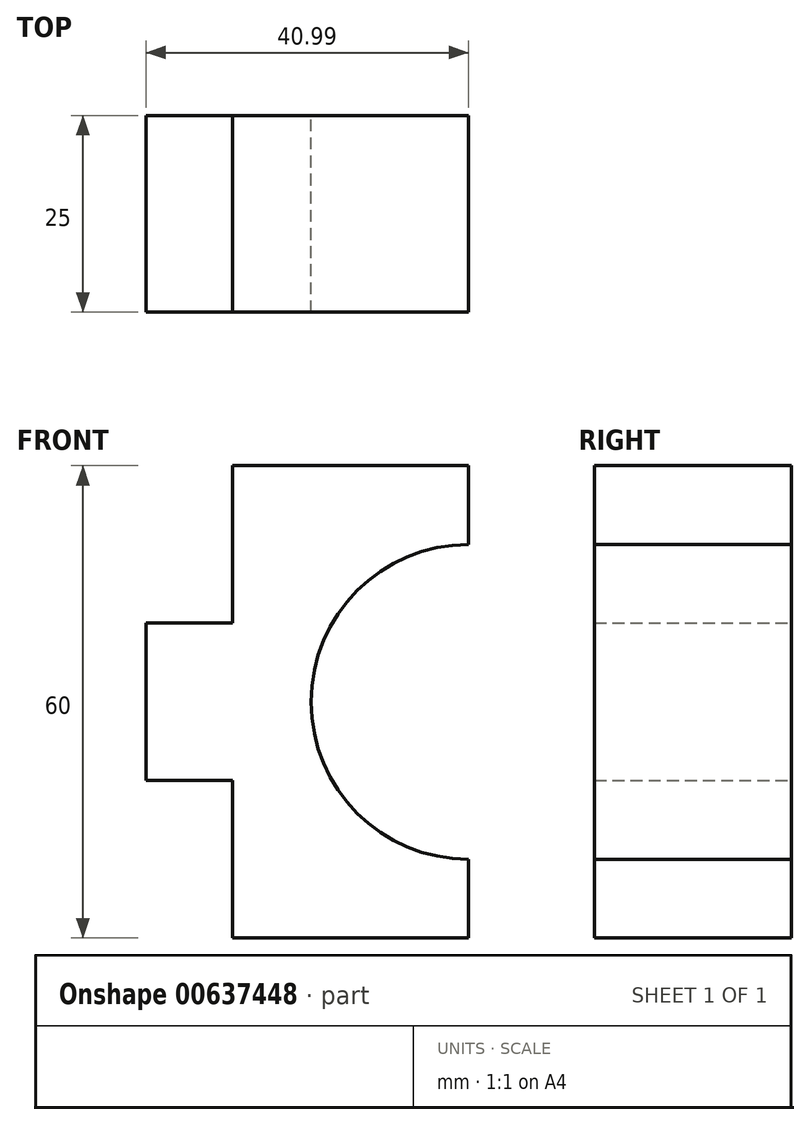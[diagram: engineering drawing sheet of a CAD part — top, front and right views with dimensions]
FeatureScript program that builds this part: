
annotation { "Feature Type Name" : "Feature", "Feature Type Description" : "" }
export const myFeature = defineFeature(function(context is Context, id is Id, definition is map)
    precondition{}
    {
        {
            var Q0;
            Q0=qCreatedBy(makeId("Front.planeOp"),FACE);
            var sketch = newSketch(context, id + "F0", { "sketchPlane" : qUnion([Q0])});
            skLineSegment(sketch, "E0.bottom", {"start": v(-45.84, 60) * mm, "end": v(-15.84, 60) * mm});
            skLineSegment(sketch, "E0.top", {"start": v(-45.84, 0) * mm, "end": v(-15.84, 0) * mm});
            skLineSegment(sketch, "E0.left", {"start": v(-45.84, 60) * mm, "end": v(-45.84, 40) * mm});
            skLineSegment(sketch, "E0.right", {"start": v(-15.84, 60) * mm, "end": v(-15.84, 50) * mm});
            skLineSegment(sketch, "E1", {"start": v(-45.84, 40) * mm, "end": v(-56.83, 40) * mm});
            skLineSegment(sketch, "E2", {"start": v(-56.83, 40) * mm, "end": v(-56.83, 20) * mm});
            skLineSegment(sketch, "E3", {"start": v(-56.83, 20) * mm, "end": v(-45.84, 20) * mm});
            skArc(sketch, "E4", {"start": v(-15.84, 50) * mm, "mid": v(-35.84, 30) * mm, "end": v(-15.84, 10) * mm});
            skLineSegment(sketch, "E5.trimOffspring", {"start": v(-45.84, 20) * mm, "end": v(-45.84, 0) * mm});
            skLineSegment(sketch, "E6.trimOffspring", {"start": v(-15.84, 10) * mm, "end": v(-15.84, 0) * mm});
            skSolve(sketch);
        }
        {
            var Q0;
            Q0 = qSketchRegion(id + "F0", true);
            extrude(context, id + "F1", {"entities" : qUnion([Q0]), "depth" : 25 * mm, "offsetDistance" : 25 * mm});
        }
    });
